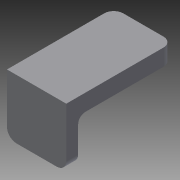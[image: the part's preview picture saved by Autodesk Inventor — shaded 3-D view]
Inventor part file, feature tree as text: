
AUTODESK INVENTOR PART (.ipt)
format: ipt  version: 2015 (Build 190159000, 159)  size: 94,208 bytes
history: native  units: mm
features: fillet x4, extrude x2, sketch x2
ambient origin geometry x8: Origin, YZ Plane, XZ Plane, XY Plane, X Axis, Y Axis, Z Axis, Center Point
bodies: Solid1 (feature_tree)
feature tree (8):
  extrude  "Extrusion1"  Depth=25.0mm
  extrude  "Extrusion2"  Depth=7.0mm
  fillet  "Fillet1"  Radius=40.0mm
  fillet  "Fillet2"  Radius=3.0mm
  fillet  "Fillet3"  Radius=4.0mm
  fillet  "Fillet4"  Radius=4.0mm
  sketch  "Sketch1"  dims[d0=25.0mm d1=25.0mm]
  sketch  "Sketch2"  dims[d2=5.0mm d3=0.0mm d4=7.0mm d5=40.0mm d6=0.0mm d7=3.0mm d8=4.0mm d9=4.0mm d10=4.0mm]
